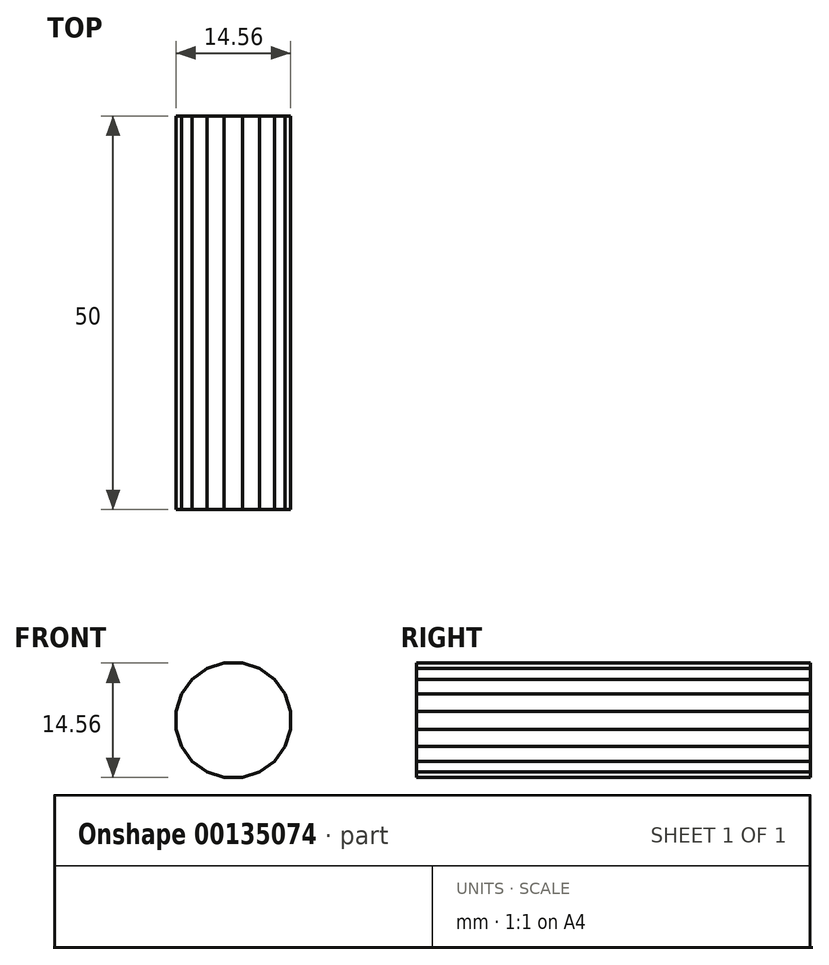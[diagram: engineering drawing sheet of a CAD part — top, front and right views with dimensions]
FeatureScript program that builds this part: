
annotation { "Feature Type Name" : "Feature", "Feature Type Description" : "" }
export const myFeature = defineFeature(function(context is Context, id is Id, definition is map)
    precondition{}
    {
        {
            var Q0;
            Q0=qCreatedBy(makeId("Front.planeOp"),FACE);
            var sketch = newSketch(context, id + "F0", { "sketchPlane" : qUnion([Q0])});
            skCircle(sketch, "E0.cCircle", {"center": v(0, 0) * mm, "radius": 7.28 * mm, "construction": true});
            skLineSegment(sketch, "E0.0", {"start": v(1.15, -7.28) * mm, "end": v(-1.15, -7.28) * mm});
            skLineSegment(sketch, "E0.1", {"start": v(-1.15, -7.28) * mm, "end": v(-3.35, -6.57) * mm});
            skLineSegment(sketch, "E0.2", {"start": v(-3.35, -6.57) * mm, "end": v(-5.21, -5.21) * mm});
            skLineSegment(sketch, "E0.3", {"start": v(-5.21, -5.21) * mm, "end": v(-6.57, -3.35) * mm});
            skLineSegment(sketch, "E0.4", {"start": v(-6.57, -3.35) * mm, "end": v(-7.28, -1.15) * mm});
            skLineSegment(sketch, "E0.5", {"start": v(-7.28, -1.15) * mm, "end": v(-7.28, 1.15) * mm});
            skLineSegment(sketch, "E0.6", {"start": v(-7.28, 1.15) * mm, "end": v(-6.57, 3.35) * mm});
            skLineSegment(sketch, "E0.7", {"start": v(-6.57, 3.35) * mm, "end": v(-5.21, 5.21) * mm});
            skLineSegment(sketch, "E0.8", {"start": v(-5.21, 5.21) * mm, "end": v(-3.35, 6.57) * mm});
            skLineSegment(sketch, "E0.9", {"start": v(-3.35, 6.57) * mm, "end": v(-1.15, 7.28) * mm});
            skLineSegment(sketch, "E0.10", {"start": v(-1.15, 7.28) * mm, "end": v(1.15, 7.28) * mm});
            skLineSegment(sketch, "E0.11", {"start": v(1.15, 7.28) * mm, "end": v(3.35, 6.57) * mm});
            skLineSegment(sketch, "E0.12", {"start": v(3.35, 6.57) * mm, "end": v(5.21, 5.21) * mm});
            skLineSegment(sketch, "E0.13", {"start": v(5.21, 5.21) * mm, "end": v(6.57, 3.35) * mm});
            skLineSegment(sketch, "E0.14", {"start": v(6.57, 3.35) * mm, "end": v(7.28, 1.15) * mm});
            skLineSegment(sketch, "E0.15", {"start": v(7.28, 1.15) * mm, "end": v(7.28, -1.15) * mm});
            skLineSegment(sketch, "E0.16", {"start": v(7.28, -1.15) * mm, "end": v(6.57, -3.35) * mm});
            skLineSegment(sketch, "E0.17", {"start": v(6.57, -3.35) * mm, "end": v(5.21, -5.21) * mm});
            skLineSegment(sketch, "E0.18", {"start": v(5.21, -5.21) * mm, "end": v(3.35, -6.57) * mm});
            skLineSegment(sketch, "E0.19", {"start": v(3.35, -6.57) * mm, "end": v(1.15, -7.28) * mm});
            skPoint(sketch, "E0.0.midPoint", {"position": v(0, -7.28) * mm});
            skSolve(sketch);
        }
        {
            var Q0;
            Q0=makeQuery(id+"F0.imprint","IMPRINT",FACE,{"disambiguationData":[TD([[makeQuery(id+"F0.imprint","IMPRINT",EDGE,{"derivedFrom":sQuery(id+"F0.wireOp",EDGE,"E0.0")}),-1.0]])]});
            extrude(context, id + "F1", {"entities" : qUnion([Q0]), "depth" : 50 * mm});
        }
    });
